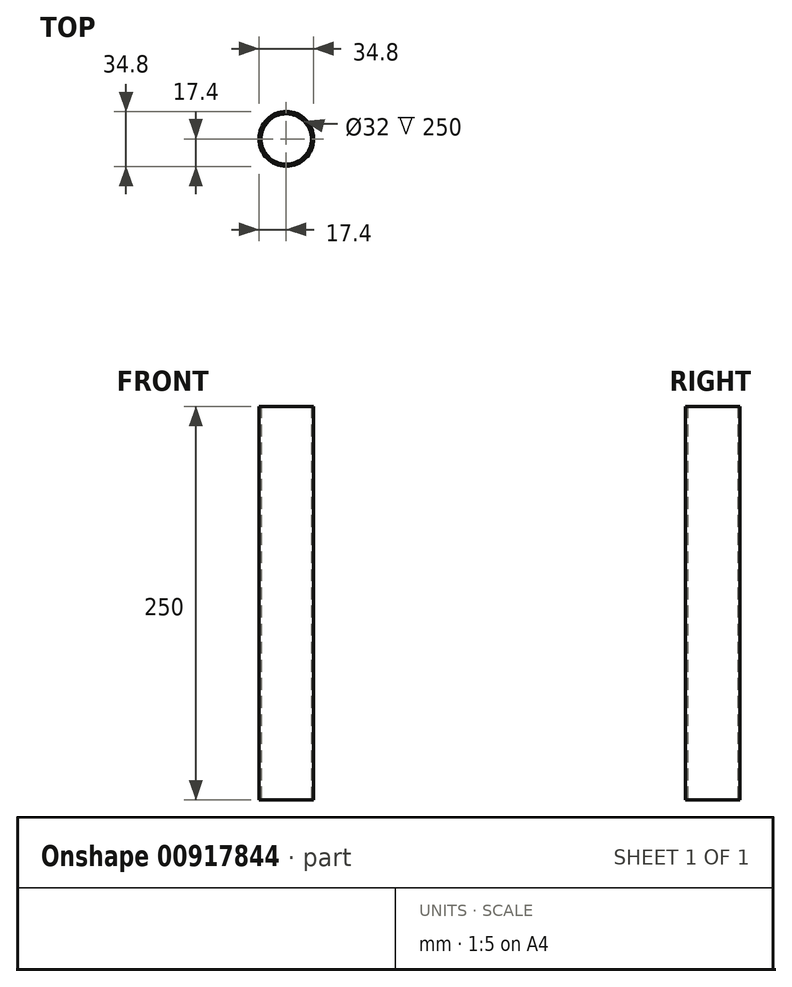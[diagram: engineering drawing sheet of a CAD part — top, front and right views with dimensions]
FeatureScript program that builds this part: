
annotation { "Feature Type Name" : "Feature", "Feature Type Description" : "" }
export const myFeature = defineFeature(function(context is Context, id is Id, definition is map)
    precondition{}
    {
        {
            var Q0;
            Q0=qCreatedBy(makeId("Top.planeOp"),FACE);
            var sketch = newSketch(context, id + "F0", { "sketchPlane" : qUnion([Q0])});
            skCircle(sketch, "E0", {"center": v(0, 0) * mm, "radius": 17.4 * mm});
            skCircle(sketch, "E1", {"center": v(0, 0) * mm, "radius": 16 * mm});
            skSolve(sketch);
        }
        {
            var Q0;
            Q0=makeQuery(id+"F0.imprint","IMPRINT",FACE,{"disambiguationData":[TD([[makeQuery(id+"F0.imprint","IMPRINT",EDGE,{"derivedFrom":sQuery(id+"F0.wireOp",EDGE,"E0")}),1.0]])]});
            extrude(context, id + "F1", {"entities" : qUnion([Q0]), "depth" : 250 * mm, "offsetDistance" : 25 * mm});
        }
    });
